# Revit family: BC_Hitachi_Samurai-M-1824-LN-PK_LOD400_
name_source: partatom
category: Mechanical Equipment
revit_build: Autodesk Revit 2018 (Build: 20170223_1515(x64)
units: mm (PartAtom-declared; Revit-internal decimal feet)

## family parameters
Always vertical = Yes
Classification = None
Cut with Voids When Loaded = No
Part Type = Normal
Room Calculation Point = No
Round Connector Dimension = Use Diameter
Shared = No
Work Plane-Based = No

## types (2) — shared parameters
BC_OBJECT_ID = 46973
BC_OBJECT_VERSION = #31
Description = Samurai M - Heat Pump Inverter Scroll (LN version - inc. VSD Pump) RHMA 18AN-NV - RHMA 100AN-NV
Frequency = 50 Hz
Inlet Water Diameter = 51 mm
Manufacturer = Hitachi Air Conditioning Europe SAS
MasterFormat = Central HVAC Equipment
Masterformat Code = 23 70 00
Model = Samurai M - Heat Pump Inverter Scroll (LN version - inc. VSD Pump)
Nominal Voltage = 400 V
Number of Poles = 3
OmniClass code = 23-33 21 13
OmniClass description = Chillers
Operating mode = Heating+Cooling
Overall height = 2440 mm
Overall length = 2300 mm
Overall width = 1200 mm
Refrigerant Type = R410A
Uniformat = Cooling Generating Systems
Uniformat code = D3030
Water Outlet Diameter = 51 mm

## per-type parameters (varying)
| type | Airflow (High) | BC_VARIANT_ID | Coefficient of Performance (COP) | Cooling Capacity | Cooling Input Rated | Energy efficiency SCOP | Energy efficiency ratio (EER) | Heating Capacity | Heating Input Rated | Load of Refrigerant Fluid | Packing Weight | Rated Cooling Current | SEER energy efficiency | Sound Power Low Noise (Cooling) | Sound Power Low Noise (Heating) | Sound Pressure at 10m (Cooling) | Sound Pressure at 1m (Cooling) | Starting current | Weight in operation |
| RHMA 24AN-NV | 4598.9 L/s | 294269 | 3.01 | 56700 W | 19600 W | 3.45 | 2.89 | 55100 W | 18300 W | 12.30 kg | 826.00 kg | 38 A | 4.71 | 77 | 76 | 48 | 63 | 108 A | 805.00 kg |
| RHMA 18AN-NV | 4185.6 L/s | 294268 | 2.99 | 41100 W | 14100 W | 3.43 | 2.92 | 45400 W | 15200 W | 9.50 kg | 806.00 kg | 29 A | 4.61 | 75 | 72 | 46 | 61 | 90 A | 782.00 kg |

note: column(s) folded — value = type name in every type: Product Code, Reference
